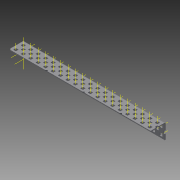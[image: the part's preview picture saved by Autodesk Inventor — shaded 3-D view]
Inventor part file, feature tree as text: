
AUTODESK INVENTOR PART (.ipt)
format: ipt  version: 2015 (Build 190159000, 159)  size: 2,203,648 bytes
history: native  units: in
note: dims shown in document units (in); Inventor stores cm internally (conversion verified against a paired STEP export)
features: other x119, pattern_linear x4, sheet_metal_op x1, extrude x1, imported_body x1, sketch x1
ambient origin geometry x8: Origin, YZ Plane, XZ Plane, XY Plane, X Axis, Y Axis, Z Axis, Center Point
bodies: Body1 (feature_tree)
feature tree (127):
  sheet_metal_op  "Fold1"
  other  "L-Channel"
  extrude  "length cut"  Depth=0.5in
  other  "top out axis"
  other  "top inner axis"
  other  "back out axis"
  other  "back inner axis"
  pattern_linear  "top outer axes"  Count1=2 Spacing1=0.5in
  pattern_linear  "top inner axes"  Spacing1=0.5in  [1 undecoded]
  pattern_linear  "back outer axes"  Count1=2 Spacing1=0.5in
  pattern_linear  "back inner axes"  Spacing1=0.5in  [1 undecoded]
  other  "right plane"
  imported_body  "Base1"
  sketch  "Sketch1"  dims[d1=0.0in d4=0.5in d5=0.7874in d7=0.5in d10=0.5in d13=0.5in d14=0.7874in d16=0.5in d19=0.5in d20=-9.5in d21=0.0in d22=0.0in d23=0.0in d24=0.0in d25=0.0in d26=0.0in]
  other  "Work Point1"
  other  "Work Point2"
  other  "Work Point3"
  other  "Work Point4"
  other  "Work Axis5"
  other  "Work Axis6"
  other  "Work Axis7"
  other  "Work Axis8"
  other  "Work Axis11"
  other  "Work Axis12"
  other  "Work Axis13"
  other  "Work Axis14"
  other  "Work Axis15"
  other  "Work Axis18"
  other  "Work Axis19"
  other  "Work Axis20"
  other  "Work Axis23"
  other  "Work Axis24"
  other  "Work Axis25"
  other  "Work Axis26"
  other  "Work Axis29"
  other  "Work Axis30"
  other  "Work Axis31"
  other  "Work Axis32"
  other  "Work Axis33"
  other  "Work Axis36"
  other  "Work Axis37"
  other  "Work Axis38"
  other  "Work Axis41"
  other  "Work Axis42"
  other  "Work Axis43"
  other  "Work Axis44"
  other  "Work Axis45"
  other  "Work Axis46"
  other  "Work Axis47"
  other  "Work Axis48"
  other  "Work Axis49"
  other  "Work Axis50"
  other  "Work Axis51"
  other  "Work Axis52"
  other  "Work Axis53"
  other  "Work Axis54"
  other  "Work Axis61"
  other  "Work Axis62"
  other  "Work Axis63"
  other  "Work Axis64"
  other  "Work Axis65"
  other  "Work Axis66"
  other  "Work Axis67"
  other  "Work Axis68"
  other  "Work Axis69"
  other  "Work Axis70"
  other  "Work Axis71"
  other  "Work Axis72"
  other  "Work Axis73"
  other  "Work Axis74"
  other  "Work Axis81"
  other  "Work Axis82"
  other  "Work Axis83"
  other  "Work Axis84"
  other  "Work Axis85"
  other  "Work Axis86"
  other  "Work Axis87"
  other  "Work Axis88"
  other  "Work Axis89"
  other  "Work Axis90"
  other  "Work Axis91"
  other  "Work Axis92"
  other  "Work Axis93"
  other  "Work Axis94"
  other  "Work Axis101"
  other  "Work Axis102"
  other  "Work Axis103"
  other  "Work Axis104"
  other  "Work Axis105"
  other  "Work Axis106"
  other  "Work Axis107"
  other  "Work Axis108"
  other  "Work Axis109"
  other  "Work Axis110"
  other  "Work Axis111"
  other  "Work Axis112"
  other  "Work Axis113"
  other  "Work Axis114"
  other  "Work Axis121"
  other  "Work Axis122"
  other  "Work Axis123"
  other  "Work Axis124"
  other  "Work Axis125"
  other  "Work Axis126"
  other  "Work Axis127"
  other  "Work Axis128"
  other  "Work Axis129"
  other  "Work Axis130"
  other  "Work Axis131"
  other  "Work Axis132"
  other  "Work Axis133"
  other  "Work Axis134"
  other  "Work Axis141"
  other  "Work Axis142"
  other  "Work Axis143"
  other  "Work Axis144"
  other  "Work Axis145"
  other  "Work Axis146"
  other  "Work Axis147"
  other  "Work Axis148"
  other  "Work Axis149"
  other  "Work Axis150"
  other  "Work Axis151"
  other  "Work Axis152"
  other  "Work Axis153"
  other  "Work Axis154"
  other  "left plane"
note: 2 required parameter values undecoded (feature->parameter linkage not recoverable at this tier; creation-order binding heuristic only, values carry confidence <= 0.55)
